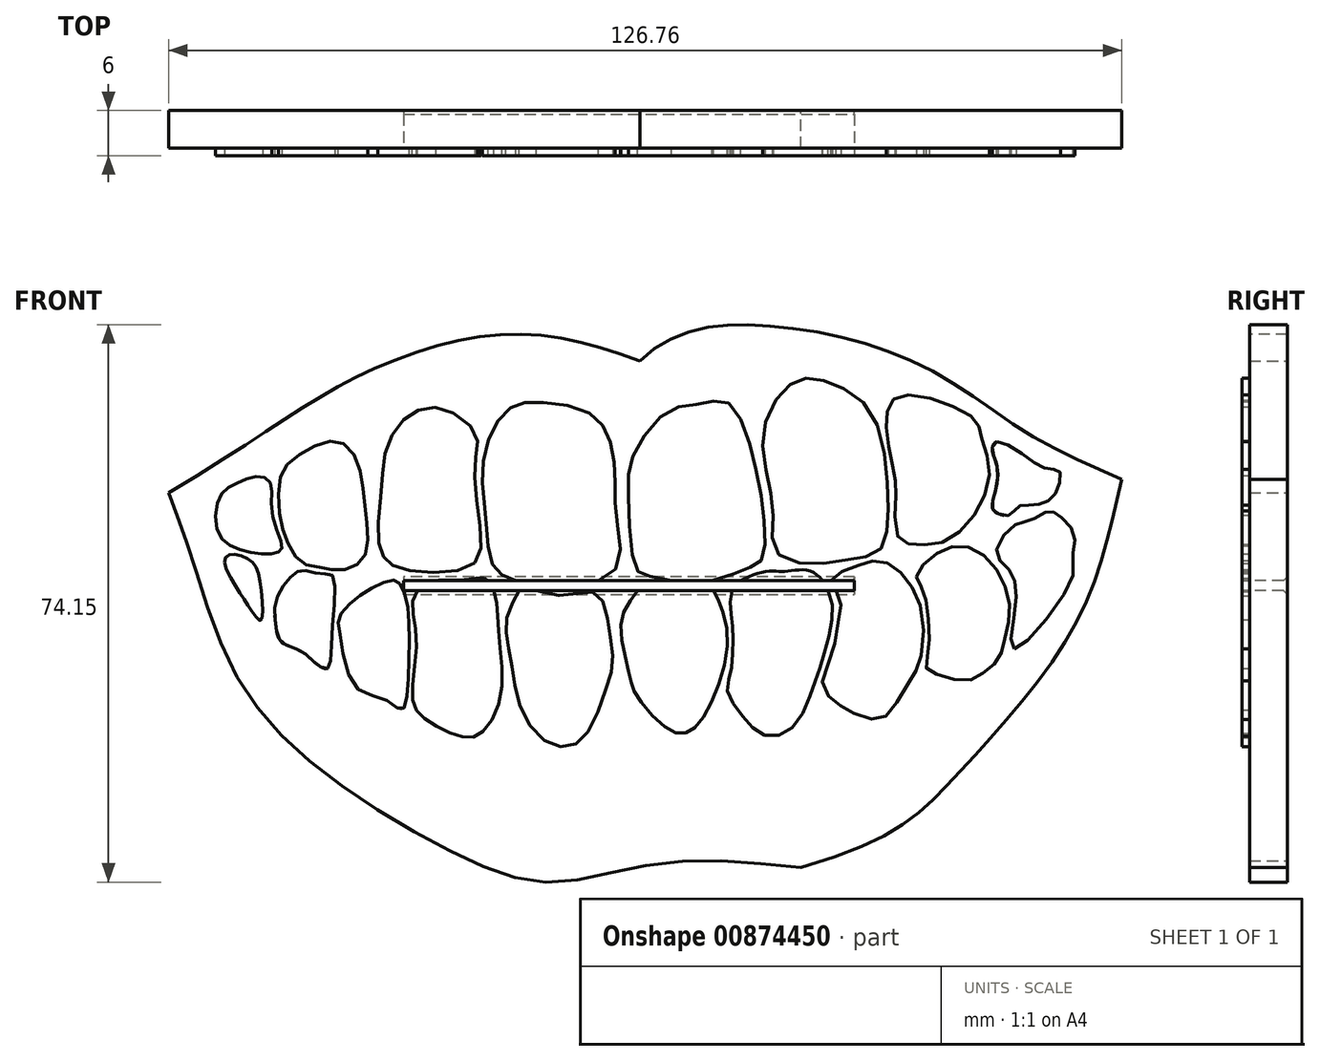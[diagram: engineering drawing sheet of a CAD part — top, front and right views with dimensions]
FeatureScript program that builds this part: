
annotation { "Feature Type Name" : "Feature", "Feature Type Description" : "" }
export const myFeature = defineFeature(function(context is Context, id is Id, definition is map)
    precondition{}
    {
        {
            var Q0;
            Q0=qCreatedBy(makeId("Front.planeOp"),FACE);
            var sketch = newSketch(context, id + "F0", { "sketchPlane" : qUnion([Q0])});
            skFitSpline(sketch, "E0", {"points": [v(0, 53.18) * mm, v(23.75, 67.94) * mm, v(44.07, 74.21) * mm, v(62.66, 70.72) * mm], "startDerivative": vector(93.7, 55.72) * mm, "endDerivative": vector(60.4, -23.03) * mm});
            skFitSpline(sketch, "E1", {"points": [v(126.76, 54.96) * mm, v(114.63, 60.86) * mm, v(103.77, 68.1) * mm, v(91.61, 73.34) * mm, v(78.85, 75.44) * mm, v(69.82, 74.76) * mm, v(62.66, 70.72) * mm], "startDerivative": vector(-69.64, 30.18) * mm, "endDerivative": vector(-38.87, -41.98) * mm});
            skFitSpline(sketch, "E2", {"points": [v(0, 53.18) * mm, v(2.98, 44.84) * mm, v(8.86, 29.1) * mm, v(20.03, 16.48) * mm, v(38.15, 5.15) * mm, v(51.1, 1.38) * mm, v(65.34, 3.9) * mm, v(84.07, 3.33) * mm], "startDerivative": vector(26.52, -69.74) * mm, "endDerivative": vector(123.22, -12.78) * mm});
            skFitSpline(sketch, "E3", {"points": [v(126.76, 54.96) * mm, v(120.46, 35.47) * mm, v(105, 15.84) * mm, v(84.07, 3.33) * mm], "startDerivative": vector(-14.9, -62.4) * mm, "endDerivative": vector(-111.82, -31.62) * mm});
            skSolve(sketch);
        }
        {
            var Q0;
            Q0 = qSketchRegion(id + "F0", true);
            extrude(context, id + "F1", {"entities" : qUnion([Q0]), "depth" : 5 * mm, "offsetDistance" : 25 * mm});
        }
        {
            var Q0;
            Q0=qCreatedBy(makeId("Front.planeOp"),FACE);
            var sketch = newSketch(context, id + "F2", { "sketchPlane" : qUnion([Q0])});
            skFitSpline(sketch, "E4", {"points": [v(13.53, 54.53) * mm, v(13.72, 50.73) * mm, v(15.07, 46.21) * mm, v(14.78, 45.4) * mm, v(12.9, 45.02) * mm, v(9.13, 45.7) * mm, v(6.62, 47.84) * mm, v(6.75, 52.55) * mm, v(8.76, 54.31) * mm, v(11.77, 55.38) * mm, v(13.53, 54.53) * mm]});
            skFitSpline(sketch, "E5", {"points": [v(15.91, 46.46) * mm, v(17.67, 43.89) * mm, v(20.06, 43.26) * mm, v(22.32, 42.88) * mm, v(24.83, 43.48) * mm, v(26.34, 45.36) * mm, v(26.34, 49.16) * mm, v(25.91, 53.4) * mm, v(24.95, 57.73) * mm, v(22.6, 60.01) * mm, v(19.54, 59.41) * mm, v(16.05, 57.19) * mm, v(14.73, 54.54) * mm, v(14.85, 49.67) * mm, v(15.91, 46.46) * mm]});
            skFitSpline(sketch, "E6", {"points": [v(28.62, 44.69) * mm, v(29.89, 43.48) * mm, v(34.59, 42.6) * mm, v(40.26, 43.48) * mm, v(41.53, 46.18) * mm, v(40.86, 52.9) * mm, v(40.86, 57.98) * mm, v(40.94, 60.82) * mm, v(37.58, 63.95) * mm, v(34, 64.4) * mm, v(31, 62.61) * mm, v(28.91, 58.88) * mm, v(28.32, 53.8) * mm, v(27.87, 47.23) * mm, v(28.62, 44.69) * mm]});
            skFitSpline(sketch, "E7", {"points": [v(44.52, 42.15) * mm, v(48.03, 41.1) * mm, v(54.6, 40.88) * mm, v(59.68, 43.48) * mm, v(59.53, 50.07) * mm, v(59.38, 55.52) * mm, v(58.48, 60.67) * mm, v(55.8, 63.88) * mm, v(48.94, 65.26) * mm, v(45.8, 64.69) * mm, v(42.94, 61.26) * mm, v(41.71, 55.2) * mm, v(42.18, 49.9) * mm, v(42.88, 44.16) * mm, v(44.52, 42.15) * mm]});
            skFitSpline(sketch, "E8", {"points": [v(62.1, 43.24) * mm, v(63.7, 42.16) * mm, v(70.98, 41.29) * mm, v(76.92, 43.14) * mm, v(78.87, 44.25) * mm, v(79.15, 50) * mm, v(77.48, 58.9) * mm, v(74.32, 65.2) * mm, v(70.8, 65.02) * mm, v(66.53, 64.1) * mm, v(61.8, 58.16) * mm, v(61.16, 52.97) * mm, v(62.1, 43.24) * mm]});
            skFitSpline(sketch, "E9", {"points": [v(84.75, 68.4) * mm, v(81.88, 66.9) * mm, v(79.19, 61.72) * mm, v(79.56, 55.52) * mm, v(80.4, 49.9) * mm, v(80.67, 45.49) * mm, v(85.3, 43.73) * mm, v(90.69, 44.38) * mm, v(94.4, 45.4) * mm, v(95.6, 48.73) * mm, v(95.51, 55.52) * mm, v(93.28, 64.1) * mm, v(88.46, 67.65) * mm, v(84.75, 68.4) * mm]});
            skFitSpline(sketch, "E10", {"points": [v(96.73, 52.86) * mm, v(97, 47.25) * mm, v(99.29, 46.31) * mm, v(103.34, 46.8) * mm, v(107.76, 51.18) * mm, v(109.12, 56.92) * mm, v(107.97, 60.88) * mm, v(107.42, 62.7) * mm, v(102.85, 65.25) * mm, v(97.09, 66) * mm, v(95.6, 64.1) * mm, v(95.6, 60.25) * mm, v(96.52, 55.52) * mm, v(96.73, 52.86) * mm]});
            skFitSpline(sketch, "E11", {"points": [v(110.18, 59.97) * mm, v(114.14, 57.92) * mm, v(117.02, 56.33) * mm, v(118.46, 56.1) * mm, v(118.25, 53.68) * mm, v(116.74, 51.94) * mm, v(114.5, 51.53) * mm, v(112.9, 51.3) * mm, v(112, 50.26) * mm, v(110.2, 50.45) * mm, v(109.56, 51.32) * mm, v(110.06, 53.92) * mm, v(110.15, 56.8) * mm, v(109.52, 59.03) * mm, v(110.18, 59.97) * mm]});
            skFitSpline(sketch, "E12", {"points": [v(11.17, 43.89) * mm, v(12.2, 41.1) * mm, v(12.24, 36.22) * mm, v(11.06, 37.44) * mm, v(9.13, 40.43) * mm, v(7.44, 44.3) * mm, v(8.64, 45.02) * mm, v(11.17, 43.89) * mm]});
            skFitSpline(sketch, "E13", {"points": [v(21.14, 29.83) * mm, v(21.72, 34.48) * mm, v(21.79, 42.16) * mm, v(20.1, 42.4) * mm, v(17.67, 42.88) * mm, v(16.05, 41.78) * mm, v(14.24, 38.78) * mm, v(14.3, 35.25) * mm, v(15.07, 33.28) * mm, v(17.67, 32.08) * mm, v(19.72, 30.35) * mm, v(21.14, 29.83) * mm]});
            skFitSpline(sketch, "E14", {"points": [v(30.73, 41.1) * mm, v(31.74, 38.4) * mm, v(31.98, 33.3) * mm, v(31.73, 26.51) * mm, v(31, 24.29) * mm, v(28.91, 25.6) * mm, v(24.83, 27.42) * mm, v(22.77, 34.48) * mm, v(22.7, 36.6) * mm, v(24.54, 38.83) * mm, v(27.44, 40.73) * mm, v(29.89, 41.6) * mm, v(30.73, 41.1) * mm]});
            skFitSpline(sketch, "E15", {"points": [v(42.2, 41.68) * mm, v(43.53, 39.08) * mm, v(43.93, 34.2) * mm, v(44.07, 25.72) * mm, v(41.16, 20.94) * mm, v(38.36, 20.92) * mm, v(33.92, 23.23) * mm, v(32.45, 25.84) * mm, v(32.94, 33.79) * mm, v(32.49, 38.99) * mm, v(34.7, 41.3) * mm, v(39.33, 41.6) * mm, v(42.2, 41.68) * mm]});
            skFitSpline(sketch, "E16", {"points": [v(47.25, 40.47) * mm, v(52.4, 39.48) * mm, v(55.99, 40.03) * mm, v(57.7, 38.78) * mm, v(58.62, 34.68) * mm, v(59.1, 30.71) * mm, v(58.05, 26.74) * mm, v(55.52, 21) * mm, v(52.99, 19.42) * mm, v(49.52, 20.54) * mm, v(46.48, 25.63) * mm, v(45.68, 30.17) * mm, v(44.97, 33.94) * mm, v(45.02, 36.7) * mm, v(46.29, 39.65) * mm, v(47.25, 40.47) * mm]});
            skFitSpline(sketch, "E17", {"points": [v(62.1, 26.4) * mm, v(65.59, 22.35) * mm, v(68.22, 21.16) * mm, v(70.18, 22.1) * mm, v(72.87, 26.9) * mm, v(74.31, 34.2) * mm, v(73.13, 38.88) * mm, v(72.04, 40.46) * mm, v(67.8, 40.35) * mm, v(63.63, 41.25) * mm, v(62, 39.64) * mm, v(60.28, 36.67) * mm, v(60.56, 32.18) * mm, v(61.47, 28.08) * mm, v(62.1, 26.4) * mm]});
            skFitSpline(sketch, "E18", {"points": [v(75.5, 41.02) * mm, v(74.65, 38.62) * mm, v(74.97, 35.94) * mm, v(75.02, 32.76) * mm, v(74.73, 29.26) * mm, v(74.31, 26.9) * mm, v(76.28, 23.51) * mm, v(79.22, 20.96) * mm, v(82.79, 21.8) * mm, v(85.58, 26.9) * mm, v(86.81, 30.54) * mm, v(88.12, 35.59) * mm, v(87.94, 39.62) * mm, v(85.4, 42.75) * mm, v(82.06, 42.72) * mm, v(79.69, 42.72) * mm, v(75.5, 41.02) * mm]});
            skFitSpline(sketch, "E19", {"points": [v(88.12, 41.63) * mm, v(89.22, 39.45) * mm, v(89.15, 36.51) * mm, v(88.12, 31.49) * mm, v(86.94, 27.61) * mm, v(88.64, 25.34) * mm, v(90.8, 24.02) * mm, v(94.25, 23.02) * mm, v(96.37, 24.55) * mm, v(98.81, 28.54) * mm, v(99.9, 30.62) * mm, v(100.18, 37.32) * mm, v(98.19, 41.57) * mm, v(95.75, 43.77) * mm, v(93.22, 44.03) * mm, v(90.69, 43.13) * mm, v(88.12, 41.63) * mm]});
            skFitSpline(sketch, "E20", {"points": [v(99.44, 41.98) * mm, v(101.2, 44.38) * mm, v(104.48, 46.05) * mm, v(107.95, 45.2) * mm, v(110.88, 41.6) * mm, v(111.85, 37.32) * mm, v(111.18, 33.59) * mm, v(110.42, 31.17) * mm, v(108.52, 29.32) * mm, v(106.28, 28.2) * mm, v(102.13, 29.03) * mm, v(100.73, 29.97) * mm, v(101.09, 32.23) * mm, v(100.9, 37.32) * mm, v(100.18, 40.58) * mm, v(99.44, 41.98) * mm]});
            skFitSpline(sketch, "E21", {"points": [v(112.46, 32.44) * mm, v(120.07, 41.6) * mm, v(120.21, 44.38) * mm, v(120.43, 47.74) * mm, v(118.2, 50.28) * mm, v(117.02, 50.71) * mm, v(114.5, 49.43) * mm, v(112.66, 49) * mm, v(110.06, 45.2) * mm, v(111.85, 42.83) * mm, v(112.64, 38.24) * mm, v(112.46, 32.44) * mm]});
            skSolve(sketch);
        }
        {
            var Q0;
            Q0 = qSketchRegion(id + "F2", true);
            extrude(context, id + "F3", {"entities" : qUnion([Q0]), "operationType" : NewBodyOperationType.ADD, "depth" : 6 * mm, "offsetDistance" : 25 * mm});
        }
        {
            var Q0;
            Q0=makeQuery(id+"F1.opExtrude","CAP_FACE",FACE,{"disambiguationData":[OSD([sQuery(id+"F0.wireOp",EDGE,"E0"),sQuery(id+"F0.wireOp",EDGE,"E1"),sQuery(id+"F0.wireOp",EDGE,"E2"),sQuery(id+"F0.wireOp",EDGE,"E3"),sQuery(id+"F0.wireOp",EDGE,"c03cad43-ab72-49c9-a026-cb0beb410997"),sQuery(id+"F0.wireOp",EDGE,"4de34322-1c2c-4337-a2a9-45364e01a36a")])],"isStart":false});
            var sketch = newSketch(context, id + "F4", { "sketchPlane" : qUnion([Q0])});
            skLineSegment(sketch, "E22.bottom", {"start": v(31.22, 41.49) * mm, "end": v(91.22, 41.49) * mm});
            skLineSegment(sketch, "E22.top", {"start": v(31.22, 40.19) * mm, "end": v(91.22, 40.19) * mm});
            skLineSegment(sketch, "E22.left", {"start": v(31.22, 41.49) * mm, "end": v(31.22, 40.19) * mm});
            skLineSegment(sketch, "E22.right", {"start": v(91.22, 41.49) * mm, "end": v(91.22, 40.19) * mm});
            skSolve(sketch);
        }
        {
            var Q0;
            Q0 = qSketchRegion(id + "F4", true);
            extrude(context, id + "F5", {"entities" : qUnion([Q0]), "operationType" : NewBodyOperationType.REMOVE, "oppositeDirection" : true, "depth" : 25 * mm, "offsetDistance" : 25 * mm, "hasSecondDirection" : true, "secondDirectionOppositeDirection" : false, "secondDirectionDepth" : 25 * mm});
        }
        {
            var Q0;
            Q0=makeQuery(id+"F5.boolean.opBoolean","INTERSECT",EDGE,{"derivedFrom":[makeQuery(id+"F1.opExtrude","CAP_FACE",FACE,{"disambiguationData":[OSD([sQuery(id+"F0.wireOp",EDGE,"E0"),sQuery(id+"F0.wireOp",EDGE,"E1"),sQuery(id+"F0.wireOp",EDGE,"E2"),sQuery(id+"F0.wireOp",EDGE,"E3")])],"isStart":true}),makeQuery(id+"F5.opExtrude","SWEPT_FACE",FACE,{"disambiguationData":[OSD([sQuery(id+"F4.wireOp",EDGE,"E22.bottom")])]})]});
            var Q1;
            Q1=makeQuery(id+"F5.boolean.opBoolean","INTERSECT",EDGE,{"derivedFrom":[makeQuery(id+"F1.opExtrude","CAP_FACE",FACE,{"disambiguationData":[OSD([sQuery(id+"F0.wireOp",EDGE,"E0"),sQuery(id+"F0.wireOp",EDGE,"E1"),sQuery(id+"F0.wireOp",EDGE,"E2"),sQuery(id+"F0.wireOp",EDGE,"E3")])],"isStart":true}),makeQuery(id+"F5.opExtrude","SWEPT_FACE",FACE,{"disambiguationData":[OSD([sQuery(id+"F4.wireOp",EDGE,"E22.top")])]})]});
            chamfer(context, id + "F6", {"entities" : qUnion([Q0, Q1]), "width" : 0.5 * mm, "tangentPropagation" : true});
        }
    });
